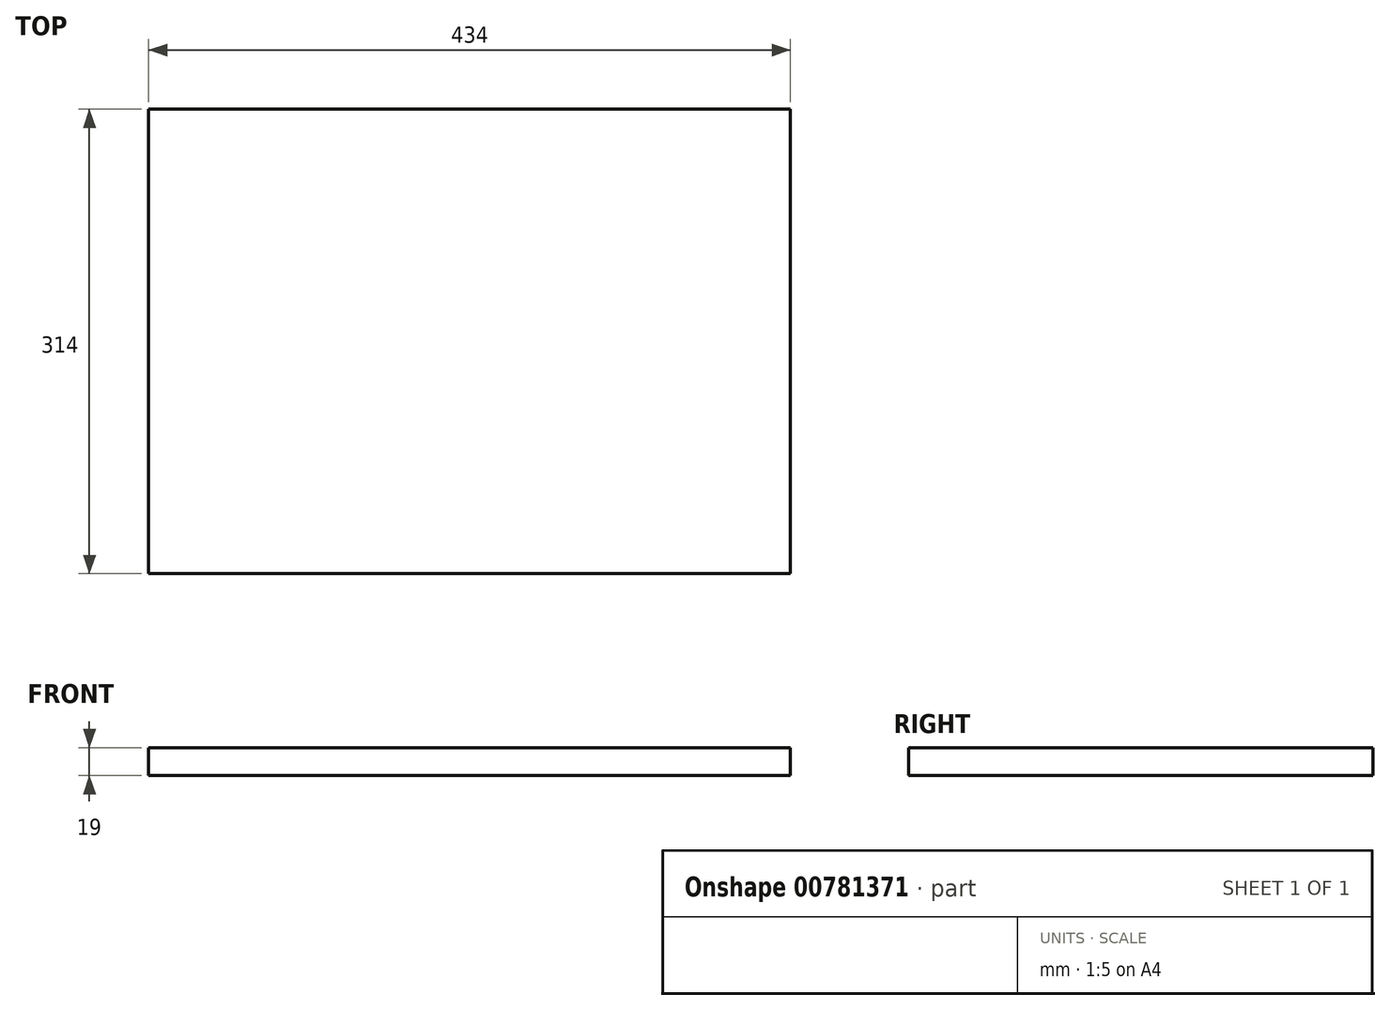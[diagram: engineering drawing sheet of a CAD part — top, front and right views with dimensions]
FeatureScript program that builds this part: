
annotation { "Feature Type Name" : "Feature", "Feature Type Description" : "" }
export const myFeature = defineFeature(function(context is Context, id is Id, definition is map)
    precondition{}
    {
        {
            var Q0;
            Q0=qCreatedBy(makeId("Top.planeOp"),FACE);
            var sketch = newSketch(context, id + "F0", { "sketchPlane" : qUnion([Q0])});
            skLineSegment(sketch, "E0.bottom", {"start": v(217, -157) * mm, "end": v(-217, -157) * mm});
            skLineSegment(sketch, "E0.top", {"start": v(217, 157) * mm, "end": v(-217, 157) * mm});
            skLineSegment(sketch, "E0.left", {"start": v(217, -157) * mm, "end": v(217, 157) * mm});
            skLineSegment(sketch, "E0.right", {"start": v(-217, -157) * mm, "end": v(-217, 157) * mm});
            skPoint(sketch, "E0.middle", {"position": v(0, 0) * mm});
            skSolve(sketch);
        }
        {
            var Q0;
            Q0=qSketchRegion(id+"F0",true);
            extrude(context, id + "F1", {"entities" : qUnion([Q0]), "depth" : 19 * mm, "offsetDistance" : 25.4 * mm});
        }
    });
